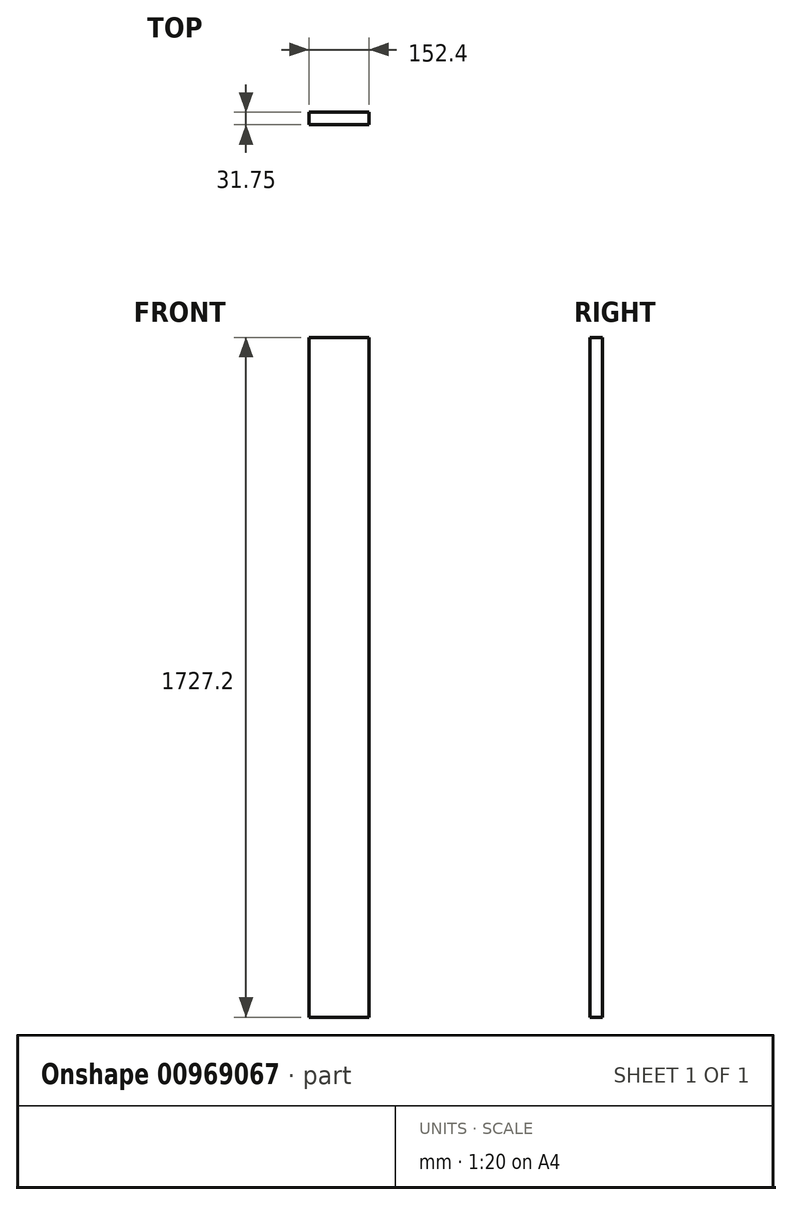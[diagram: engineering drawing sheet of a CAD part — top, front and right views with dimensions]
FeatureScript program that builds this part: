
annotation { "Feature Type Name" : "Feature", "Feature Type Description" : "" }
export const myFeature = defineFeature(function(context is Context, id is Id, definition is map)
    precondition{}
    {
        {
            var Q0;
            Q0=qCreatedBy(makeId("Top.planeOp"),FACE);
            var sketch = newSketch(context, id + "F0", { "sketchPlane" : qUnion([Q0])});
            skLineSegment(sketch, "E0.bottom", {"start": v(0, 0) * mm, "end": v(152.4, 0) * mm});
            skLineSegment(sketch, "E0.top", {"start": v(0, -31.75) * mm, "end": v(152.4, -31.75) * mm});
            skLineSegment(sketch, "E0.left", {"start": v(0, 0) * mm, "end": v(0, -31.75) * mm});
            skLineSegment(sketch, "E0.right", {"start": v(152.4, 0) * mm, "end": v(152.4, -31.75) * mm});
            skSolve(sketch);
        }
        {
            var Q0;
            Q0 = qSketchRegion(id + "F0", true);
            extrude(context, id + "F1", {"entities" : qUnion([Q0]), "depth" : 1727.2 * mm, "offsetDistance" : 25.4 * mm});
        }
    });
